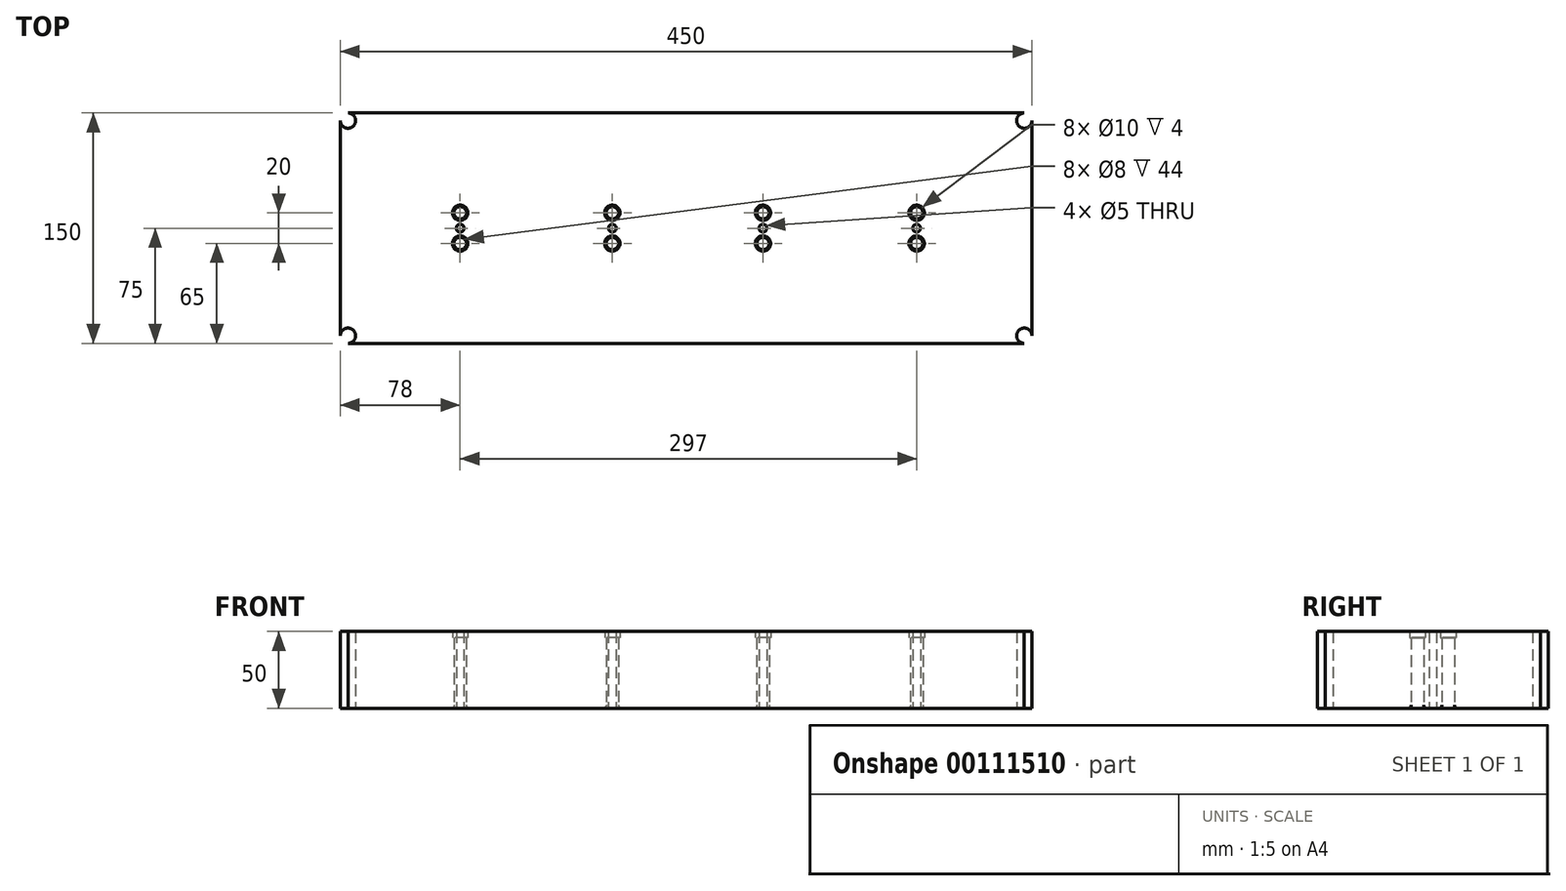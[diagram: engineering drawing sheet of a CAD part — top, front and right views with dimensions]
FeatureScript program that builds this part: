
annotation { "Feature Type Name" : "Feature", "Feature Type Description" : "" }
export const myFeature = defineFeature(function(context is Context, id is Id, definition is map)
    precondition{}
    {
        {
            var Q0;
            Q0=qCreatedBy(makeId("Top.planeOp"),FACE);
            var sketch = newSketch(context, id + "F0", { "sketchPlane" : qUnion([Q0])});
            skLineSegment(sketch, "E0.bottom", {"start": v(-225, 75) * mm, "end": v(225, 75) * mm});
            skLineSegment(sketch, "E0.top", {"start": v(-225, -75) * mm, "end": v(225, -75) * mm});
            skLineSegment(sketch, "E0.left", {"start": v(-225, 75) * mm, "end": v(-225, -75) * mm});
            skLineSegment(sketch, "E0.right", {"start": v(225, 75) * mm, "end": v(225, -75) * mm});
            skPoint(sketch, "E0.middle", {"position": v(0, 0) * mm});
            skLineSegment(sketch, "E1", {"start": v(0, 0) * mm, "end": v(-48, 0) * mm});
            skLineSegment(sketch, "E2", {"start": v(0, 0) * mm, "end": v(-147, 0) * mm});
            skLineSegment(sketch, "E3", {"start": v(0, 0) * mm, "end": v(50, 0) * mm});
            skLineSegment(sketch, "E4", {"start": v(0, 0) * mm, "end": v(150, 0) * mm});
            skPoint(sketch, "E4.endSnap0", {"position": v(25, 0) * mm});
            skCircle(sketch, "E5", {"center": v(-48, 0) * mm, "radius": 20 * mm});
            skCircle(sketch, "E6", {"center": v(-147, 0) * mm, "radius": 20 * mm});
            skCircle(sketch, "E7", {"center": v(50, 0) * mm, "radius": 20 * mm});
            skCircle(sketch, "E8", {"center": v(150, 0) * mm, "radius": 20 * mm});
            skLineSegment(sketch, "E9", {"start": v(-147, 0) * mm, "end": v(-147, 10) * mm});
            skLineSegment(sketch, "E10", {"start": v(-147, 10) * mm, "end": v(-147, 0) * mm});
            skLineSegment(sketch, "E11", {"start": v(-147, 0) * mm, "end": v(-147, -10) * mm});
            skCircle(sketch, "E12", {"center": v(-147, 10) * mm, "radius": 4 * mm});
            skCircle(sketch, "E13", {"center": v(-147, -10) * mm, "radius": 4 * mm});
            skCircle(sketch, "E14", {"center": v(-147, 0) * mm, "radius": 2.5 * mm});
            skLineSegment(sketch, "E15", {"start": v(-48, 0) * mm, "end": v(-48, 10) * mm});
            skLineSegment(sketch, "E16", {"start": v(-48, 0) * mm, "end": v(-48, -10) * mm});
            skCircle(sketch, "E17", {"center": v(-48, 10) * mm, "radius": 4 * mm});
            skCircle(sketch, "E18", {"center": v(-48, -10) * mm, "radius": 4 * mm});
            skCircle(sketch, "E19", {"center": v(-48, 0) * mm, "radius": 2.5 * mm});
            skLineSegment(sketch, "E20", {"start": v(50, 0) * mm, "end": v(50, 10) * mm});
            skLineSegment(sketch, "E21", {"start": v(50, 0) * mm, "end": v(50, -10) * mm});
            skCircle(sketch, "E22", {"center": v(50, 10) * mm, "radius": 4 * mm});
            skCircle(sketch, "E23", {"center": v(50, 0) * mm, "radius": 2.5 * mm});
            skCircle(sketch, "E24", {"center": v(50, -10) * mm, "radius": 4 * mm});
            skLineSegment(sketch, "E25", {"start": v(150, 0) * mm, "end": v(150, 10) * mm});
            skLineSegment(sketch, "E26", {"start": v(150, 0) * mm, "end": v(150, -10) * mm});
            skCircle(sketch, "E27", {"center": v(150, 10) * mm, "radius": 4 * mm});
            skCircle(sketch, "E28", {"center": v(150, 0) * mm, "radius": 2.5 * mm});
            skCircle(sketch, "E29", {"center": v(150, -10) * mm, "radius": 4 * mm});
            skCircle(sketch, "E30", {"center": v(-220, 70) * mm, "radius": 5 * mm});
            skCircle(sketch, "E31", {"center": v(-220, -70) * mm, "radius": 5 * mm});
            skCircle(sketch, "E32", {"center": v(220, -70) * mm, "radius": 5 * mm});
            skCircle(sketch, "E33", {"center": v(220, 70) * mm, "radius": 5 * mm});
            skCircle(sketch, "E34", {"center": v(-147, -10) * mm, "radius": 5 * mm});
            skCircle(sketch, "E35", {"center": v(-147, 10) * mm, "radius": 5 * mm});
            skCircle(sketch, "E36", {"center": v(-48, -10) * mm, "radius": 5 * mm});
            skCircle(sketch, "E37", {"center": v(-48, 10) * mm, "radius": 5 * mm});
            skCircle(sketch, "E38", {"center": v(50, -10) * mm, "radius": 5 * mm});
            skCircle(sketch, "E39", {"center": v(50, 10) * mm, "radius": 5 * mm});
            skCircle(sketch, "E40", {"center": v(150, -10) * mm, "radius": 5 * mm});
            skCircle(sketch, "E41", {"center": v(150, 10) * mm, "radius": 5 * mm});
            skSolve(sketch);
        }
        {
            var Q0;
            Q0=makeQuery(id+"F0.imprint","IMPRINT",FACE,{"disambiguationData":[TD([[makeQuery(id+"F0.imprint","IMPRINT",EDGE,{"derivedFrom":sQuery(id+"F0.wireOp",EDGE,"E6")}),-1.0]])]});
            var Q1;
            Q1=makeQuery(id+"F0.imprint","IMPRINT",FACE,{"disambiguationData":[TD([[makeQuery(id+"F0.imprint","IMPRINT",EDGE,{"derivedFrom":sQuery(id+"F0.wireOp",EDGE,"E6")}),1.0]])]});
            var Q2;
            Q2=makeQuery(id+"F0.imprint","IMPRINT",FACE,{"disambiguationData":[TD([[makeQuery(id+"F0.imprint","IMPRINT",EDGE,{"derivedFrom":sQuery(id+"F0.wireOp",EDGE,"E8")}),1.0]])]});
            var Q3;
            Q3=makeQuery(id+"F0.imprint","IMPRINT",FACE,{"disambiguationData":[TD([[makeQuery(id+"F0.imprint","IMPRINT",EDGE,{"derivedFrom":sQuery(id+"F0.wireOp",EDGE,"E39")}),-1.0]])]});
            var Q4;
            Q4=makeQuery(id+"F0.imprint","IMPRINT",FACE,{"disambiguationData":[TD([[makeQuery(id+"F0.imprint","IMPRINT",EDGE,{"derivedFrom":sQuery(id+"F0.wireOp",EDGE,"E38")}),-1.0]])]});
            var Q5;
            Q5=makeQuery(id+"F0.imprint","IMPRINT",FACE,{"disambiguationData":[TD([[makeQuery(id+"F0.imprint","IMPRINT",EDGE,{"derivedFrom":sQuery(id+"F0.wireOp",EDGE,"E37")}),-1.0]])]});
            var Q6;
            Q6=makeQuery(id+"F0.imprint","IMPRINT",FACE,{"disambiguationData":[TD([[makeQuery(id+"F0.imprint","IMPRINT",EDGE,{"derivedFrom":sQuery(id+"F0.wireOp",EDGE,"E36")}),-1.0]])]});
            extrude(context, id + "F1", {"entities" : qUnion([Q0, Q1, Q2, Q3, Q4, Q5, Q6]), "depth" : 50 * mm});
        }
        {
            var Q0;
            Q0=qCreatedBy(makeId("Front.planeOp"),FACE);
            var sketch = newSketch(context, id + "F2", { "sketchPlane" : qUnion([Q0])});
            skLineSegment(sketch, "E42", {"start": v(0, 0) * mm, "end": v(-225, 0) * mm});
            skLineSegment(sketch, "E43", {"start": v(0, 0) * mm, "end": v(225, 0) * mm});
            skLineSegment(sketch, "E44", {"start": v(0, 0) * mm, "end": v(0, -25) * mm});
            skSolve(sketch);
        }
        {
            var Q0;
            Q0=makeQuery(id+"F0.imprint","IMPRINT",FACE,{"disambiguationData":[TD([[makeQuery(id+"F0.imprint","IMPRINT",EDGE,{"derivedFrom":sQuery(id+"F0.wireOp",EDGE,"E12")}),-1.0]])]});
            var Q1;
            Q1=makeQuery(id+"F0.imprint","IMPRINT",FACE,{"disambiguationData":[TD([[makeQuery(id+"F0.imprint","IMPRINT",EDGE,{"derivedFrom":sQuery(id+"F0.wireOp",EDGE,"E13")}),-1.0]])]});
            var Q2;
            Q2=makeQuery(id+"F0.imprint","IMPRINT",FACE,{"disambiguationData":[TD([[makeQuery(id+"F0.imprint","IMPRINT",EDGE,{"derivedFrom":sQuery(id+"F0.wireOp",EDGE,"E17")}),-1.0]])]});
            var Q3;
            Q3=makeQuery(id+"F0.imprint","IMPRINT",FACE,{"disambiguationData":[TD([[makeQuery(id+"F0.imprint","IMPRINT",EDGE,{"derivedFrom":sQuery(id+"F0.wireOp",EDGE,"E18")}),-1.0]])]});
            var Q4;
            Q4=makeQuery(id+"F0.imprint","IMPRINT",FACE,{"disambiguationData":[TD([[makeQuery(id+"F0.imprint","IMPRINT",EDGE,{"derivedFrom":sQuery(id+"F0.wireOp",EDGE,"E24")}),-1.0]])]});
            var Q5;
            Q5=makeQuery(id+"F0.imprint","IMPRINT",FACE,{"disambiguationData":[TD([[makeQuery(id+"F0.imprint","IMPRINT",EDGE,{"derivedFrom":sQuery(id+"F0.wireOp",EDGE,"E22")}),-1.0]])]});
            var Q6;
            Q6=makeQuery(id+"F0.imprint","IMPRINT",FACE,{"disambiguationData":[TD([[makeQuery(id+"F0.imprint","IMPRINT",EDGE,{"derivedFrom":sQuery(id+"F0.wireOp",EDGE,"E27")}),-1.0]])]});
            var Q7;
            Q7=makeQuery(id+"F0.imprint","IMPRINT",FACE,{"disambiguationData":[TD([[makeQuery(id+"F0.imprint","IMPRINT",EDGE,{"derivedFrom":sQuery(id+"F0.wireOp",EDGE,"E29")}),-1.0]])]});
            extrude(context, id + "F3", {"entities" : qUnion([Q0, Q1, Q2, Q3, Q4, Q5, Q6, Q7]), "operationType" : NewBodyOperationType.ADD, "depth" : 46 * mm});
        }
        {
            var Q0;
            Q0=makeQuery(id+"F3.opExtrude","CAP_EDGE",EDGE,{"disambiguationData":[OSD([sQuery(id+"F0.wireOp",EDGE,"E13")])],"isStart":true});
            var Q1;
            Q1=makeQuery(id+"F3.opExtrude","CAP_EDGE",EDGE,{"disambiguationData":[OSD([sQuery(id+"F0.wireOp",EDGE,"E12")])],"isStart":true});
            var Q2;
            Q2=makeQuery(id+"F3.opExtrude","CAP_EDGE",EDGE,{"disambiguationData":[OSD([sQuery(id+"F0.wireOp",EDGE,"E18")])],"isStart":true});
            var Q3;
            Q3=makeQuery(id+"F3.opExtrude","CAP_EDGE",EDGE,{"disambiguationData":[OSD([sQuery(id+"F0.wireOp",EDGE,"E17")])],"isStart":true});
            var Q4;
            Q4=makeQuery(id+"F3.opExtrude","CAP_EDGE",EDGE,{"disambiguationData":[OSD([sQuery(id+"F0.wireOp",EDGE,"E24")])],"isStart":true});
            var Q5;
            Q5=makeQuery(id+"F3.opExtrude","CAP_EDGE",EDGE,{"disambiguationData":[OSD([sQuery(id+"F0.wireOp",EDGE,"E22")])],"isStart":true});
            var Q6;
            Q6=makeQuery(id+"F3.opExtrude","CAP_EDGE",EDGE,{"disambiguationData":[OSD([sQuery(id+"F0.wireOp",EDGE,"E29")])],"isStart":true});
            var Q7;
            Q7=makeQuery(id+"F3.opExtrude","CAP_EDGE",EDGE,{"disambiguationData":[OSD([sQuery(id+"F0.wireOp",EDGE,"E27")])],"isStart":true});
            fillet(context, id + "F4", {"entities" : qUnion([Q0, Q1, Q2, Q3, Q4, Q5, Q6, Q7]), "radius" : 2 * mm, "tangentPropagation" : true, "allowEdgeOverflow" : false});
        }
    });
